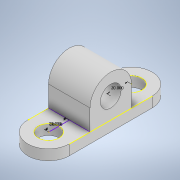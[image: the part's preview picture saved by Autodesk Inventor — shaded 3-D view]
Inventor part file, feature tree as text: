
AUTODESK INVENTOR PART (.ipt)
format: ipt  version: 2022.5 (Build 265521000, 521)  size: 148,992 bytes
history: native  units: in
note: dims shown in document units (in); Inventor stores cm internally (conversion verified against a paired STEP export)
features: sketch x11, extrude x2
ambient origin geometry x8: Origin, YZ Plane, XZ Plane, XY Plane, X Axis, Y Axis, Z Axis, Center Point
bodies: Solid1 (feature_tree)
feature tree (13):
  extrude  "Extrusion1"  Depth=40.0in
  sketch  "Sketch2"  dims[d2=80.0in d3=20.0in]
  sketch  "Sketch3"  dims[d4=20.0in]
  sketch  "Sketch4"  dims[d7=10.0in d8=0.0in]
  sketch  "Sketch5"  dims[d9=20.0in]
  sketch  "Sketch6"  dims[d10=20.0in]
  sketch  "Sketch7"  dims[d11=20.0in]
  sketch  "Sketch8"  dims[d12=20.0in]
  sketch  "Sketch9"  dims[d13=20.0in]
  sketch  "3D Sketch1"
  extrude  "Extrusion2"  Depth=20.0in
  sketch  "Sketch1"  dims[d0=80.0in d1=40.0in]
  sketch  "Sketch10"  dims[d14=40.0in d15=20.0in d16=20.0in d17=40.0in d18=0.0in d19=0.5in d20=0.0344in]
